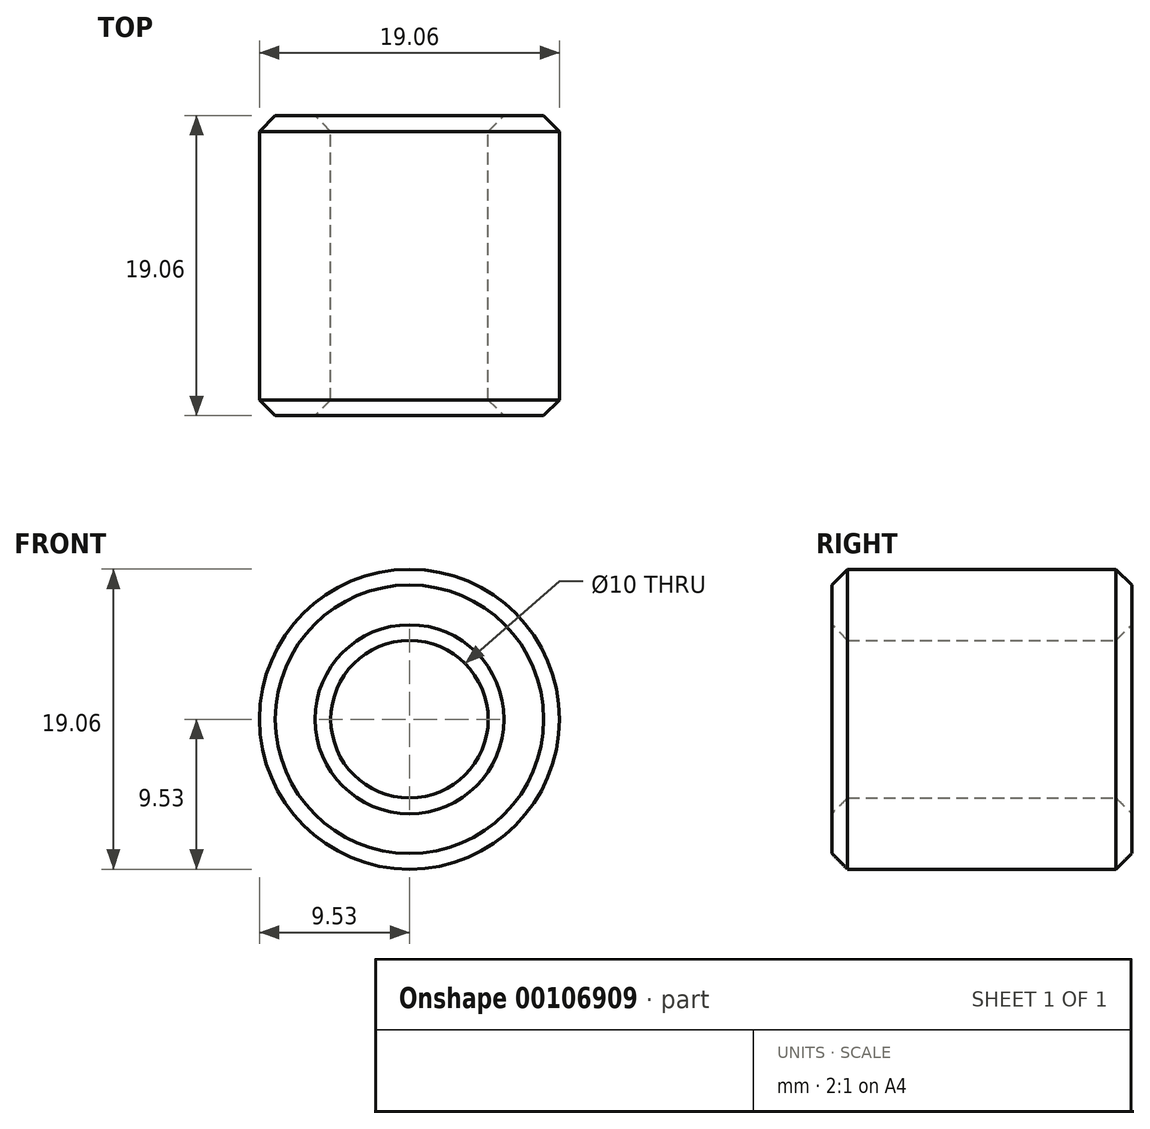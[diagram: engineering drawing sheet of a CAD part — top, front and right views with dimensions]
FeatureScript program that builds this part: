
annotation { "Feature Type Name" : "Feature", "Feature Type Description" : "" }
export const myFeature = defineFeature(function(context is Context, id is Id, definition is map)
    precondition{}
    {
        {
            var Q0;
            Q0=qCreatedBy(makeId("Front.planeOp"),FACE);
            var sketch = newSketch(context, id + "F0", { "sketchPlane" : qUnion([Q0])});
            skCircle(sketch, "E0", {"center": v(0, 0) * mm, "radius": 9.53 * mm});
            skCircle(sketch, "E1", {"center": v(0, 0) * mm, "radius": 5 * mm});
            skSolve(sketch);
        }
        {
            var Q0;
            Q0 = qSketchRegion(id + "F0", true);
            extrude(context, id + "F1", {"entities" : qUnion([Q0]), "endBound" : BoundingType.SYMMETRIC, "depth" : 19.05 * mm});
        }
        {
            var Q0;
            Q0=makeQuery(id+"F1.opExtrude","CAP_EDGE",EDGE,{"disambiguationData":[OSD([sQuery(id+"F0.wireOp",EDGE,"E0")])],"isStart":true});
            var Q1;
            Q1=makeQuery(id+"F1.opExtrude","CAP_EDGE",EDGE,{"disambiguationData":[OSD([sQuery(id+"F0.wireOp",EDGE,"E0")])],"isStart":false});
            var Q2;
            Q2=makeQuery(id+"F1.opExtrude","CAP_EDGE",EDGE,{"disambiguationData":[OSD([sQuery(id+"F0.wireOp",EDGE,"E1")])],"isStart":true});
            var Q3;
            Q3=makeQuery(id+"F1.opExtrude","CAP_EDGE",EDGE,{"disambiguationData":[OSD([sQuery(id+"F0.wireOp",EDGE,"E1")])],"isStart":false});
            chamfer(context, id + "F2", {"entities" : qUnion([Q0, Q1, Q2, Q3]), "width" : 1 * mm, "tangentPropagation" : true});
        }
    });
